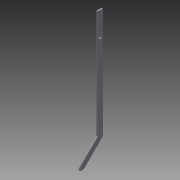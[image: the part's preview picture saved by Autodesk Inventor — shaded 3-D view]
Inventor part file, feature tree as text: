
AUTODESK INVENTOR PART (.ipt)
format: ipt  version: 2013 (Build 170138000, 138)  size: 151,040 bytes
history: native  units: in
note: dims shown in document units (in); Inventor stores cm internally (conversion verified against a paired STEP export)
features: extrude x8, sketch x7
ambient origin geometry x8: Origin, YZ Plane, XZ Plane, XY Plane, X Axis, Y Axis, Z Axis, Center Point
bodies: Solid1 (feature_tree)
feature tree (15):
  extrude  "Extrusion1"  Depth=0.5in
  extrude  "Extrusion2"  Depth=0.5in
  extrude  "Extrusion3"  Depth=16.484in
  extrude  "Extrusion4"  Depth=5.14in
  extrude  "Extrusion5"  Depth=1.0in
  extrude  "Extrusion8"  Depth=6.0in
  extrude  "Extrusion9"  Depth=1.0in
  extrude  "Extrusion11"  TaperAngle=180.0deg  [1 undecoded]
  sketch  "Sketch1"  dims[d0=0.25in d1=0.5in]
  sketch  "Sketch2"  dims[d2=0.0in d3=0.5in]
  sketch  "Sketch3"  dims[d4=90.0deg d5=16.484in]
  sketch  "Sketch4"  dims[d6=1.0in d7=5.14in]
  sketch  "Sketch5"  dims[d8=135.0deg d9=1.0in]
  sketch  "Sketch8"  dims[d10=90.0deg d11=6.0in]
  sketch  "Sketch9"  dims[d12=90.0deg d13=1.0in d14=180.0deg d15=1.0in d16=0.0in d17=0.25in d18=0.75in d19=1.0in d20=0.0in d21=5.0in d22=0.0in d23=0.75in d24=0.0in d25=1.0in d26=5.0in d27=5.0in d28=0.0in d43=4.0in d44=0.0in d45=0.5in d46=1.0in d47=0.0in d52=0.25in d53=0.0in]
note: 1 required parameter value undecoded (feature->parameter linkage not recoverable at this tier; creation-order binding heuristic only, values carry confidence <= 0.55)
